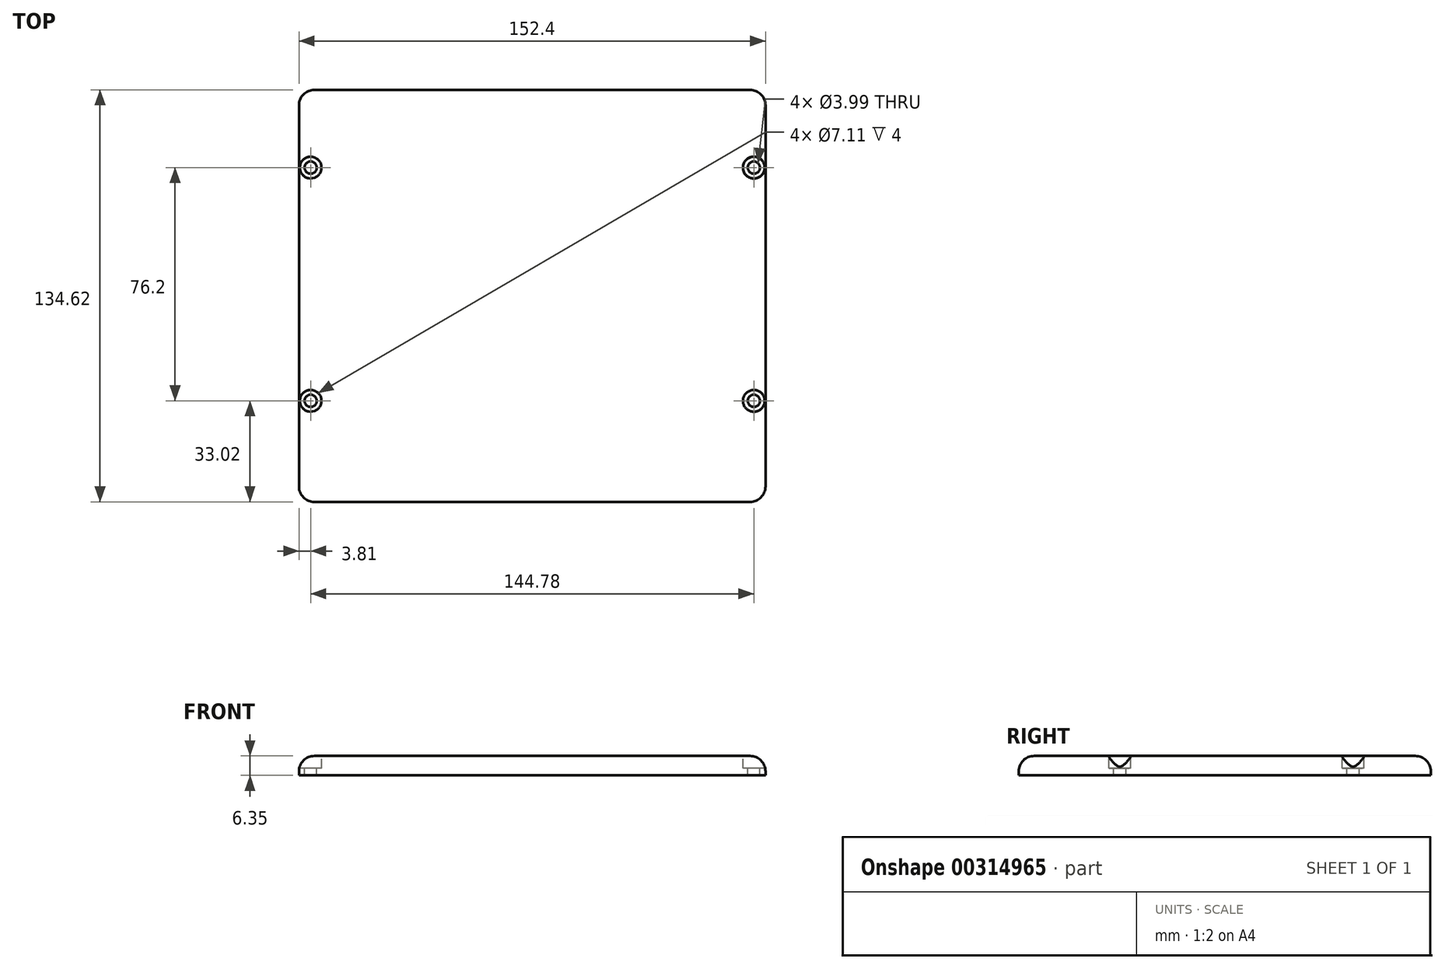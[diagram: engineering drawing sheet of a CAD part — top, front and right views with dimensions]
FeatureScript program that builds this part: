
annotation { "Feature Type Name" : "Feature", "Feature Type Description" : "" }
export const myFeature = defineFeature(function(context is Context, id is Id, definition is map)
    precondition{}
    {
        {
            var Q0;
            Q0=qCreatedBy(makeId("Top.planeOp"),FACE);
            var sketch = newSketch(context, id + "F0", { "sketchPlane" : qUnion([Q0])});
            skLineSegment(sketch, "E0.bottom", {"start": v(76.2, -67.31) * mm, "end": v(-76.2, -67.31) * mm});
            skLineSegment(sketch, "E0.top", {"start": v(76.2, 67.31) * mm, "end": v(-76.2, 67.3) * mm});
            skLineSegment(sketch, "E0.left", {"start": v(76.2, -67.31) * mm, "end": v(76.2, 67.31) * mm});
            skLineSegment(sketch, "E0.right", {"start": v(-76.2, -67.31) * mm, "end": v(-76.2, 67.3) * mm});
            skPoint(sketch, "E0.middle", {"position": v(0, 0) * mm});
            skSolve(sketch);
        }
        {
            var Q0;
            Q0=qSketchRegion(id+"F0",true);
            extrude(context, id + "F1", {"entities" : qUnion([Q0]), "depth" : 6.35 * mm});
        }
        {
            var Q0;
            Q0=makeQuery(id+"F1.opExtrude","CAP_FACE",FACE,{"disambiguationData":[OSD([sQuery(id+"F0.wireOp",EDGE,"E0.bottom"),sQuery(id+"F0.wireOp",EDGE,"E0.top"),sQuery(id+"F0.wireOp",EDGE,"E0.left"),sQuery(id+"F0.wireOp",EDGE,"E0.right")])],"isStart":false});
            var sketch = newSketch(context, id + "F2", { "sketchPlane" : qUnion([Q0])});
            skPoint(sketch, "E1", {"position": v(-72.39, 41.9) * mm});
            skPoint(sketch, "E2", {"position": v(72.4, 41.9) * mm});
            skPoint(sketch, "E3", {"position": v(72.4, -34.3) * mm});
            skPoint(sketch, "E4", {"position": v(-72.39, -34.3) * mm});
            skSolve(sketch);
        }
        {
            var Q0;
            Q0=sQuery(id+"F2.wireOp",VERTEX,"E1");
            var Q1;
            Q1=sQuery(id+"F2.wireOp",VERTEX,"E4");
            var Q2;
            Q2=sQuery(id+"F2.wireOp",VERTEX,"E3");
            var Q3;
            Q3=sQuery(id+"F2.wireOp",VERTEX,"E2");
            var Q4;
            Q4=sQuery(id+"F2.wireOp",VERTEX,"32dfac95-dade-4f80-9e21-36db3b3072a5");
            var Q5;
            Q5=makeQuery(id+"F1.opExtrude","SWEPT_BODY",BODY,{"disambiguationData":[OSD([sQuery(id+"F0.wireOp",EDGE,"E0.bottom"),sQuery(id+"F0.wireOp",EDGE,"E0.top"),sQuery(id+"F0.wireOp",EDGE,"E0.left"),sQuery(id+"F0.wireOp",EDGE,"E0.right")])]});
            hole(context, id + "F3", {"style" : HoleStyle.C_BORE, "endStyle" : HoleEndStyle.THROUGH, "holeDiameter" : 4 * mm, "cBoreDiameter" : 7.11 * mm, "cBoreDepth" : 4 * mm, "tappedDepth" : 12.7 * mm, "tapClearance" : 3, "locations" : qUnion([Q0, Q1, Q2, Q3, Q4]), "scope" : qUnion([Q5])});
        }
        {
            var Q0;
            Q0=makeQuery(id+"F1.opExtrude","CAP_EDGE",EDGE,{"disambiguationData":[OSD([sQuery(id+"F0.wireOp",EDGE,"E0.right")])],"isStart":false});
            var Q1;
            Q1=makeQuery(id+"F1.opExtrude","CAP_EDGE",EDGE,{"disambiguationData":[OSD([sQuery(id+"F0.wireOp",EDGE,"E0.top")])],"isStart":false});
            var Q2;
            Q2=makeQuery(id+"F1.opExtrude","CAP_EDGE",EDGE,{"disambiguationData":[OSD([sQuery(id+"F0.wireOp",EDGE,"E0.bottom")])],"isStart":false});
            var Q3;
            Q3=makeQuery(id+"F1.opExtrude","CAP_EDGE",EDGE,{"disambiguationData":[OSD([sQuery(id+"F0.wireOp",EDGE,"E0.left")])],"isStart":false});
            var Q4;
            Q4=makeQuery(id+"F1.opExtrude","SWEPT_EDGE",EDGE,{"disambiguationData":[OSD([sQuery(id+"F0.wireOp",EDGE,"E0.bottom"),sQuery(id+"F0.wireOp",EDGE,"E0.right")])]});
            var Q5;
            Q5=makeQuery(id+"F1.opExtrude","SWEPT_EDGE",EDGE,{"disambiguationData":[OSD([sQuery(id+"F0.wireOp",EDGE,"E0.bottom"),sQuery(id+"F0.wireOp",EDGE,"E0.left")])]});
            var Q6;
            Q6=makeQuery(id+"F1.opExtrude","SWEPT_EDGE",EDGE,{"disambiguationData":[OSD([sQuery(id+"F0.wireOp",EDGE,"E0.top"),sQuery(id+"F0.wireOp",EDGE,"E0.left")])]});
            var Q7;
            Q7=makeQuery(id+"F1.opExtrude","SWEPT_EDGE",EDGE,{"disambiguationData":[OSD([sQuery(id+"F0.wireOp",EDGE,"E0.top"),sQuery(id+"F0.wireOp",EDGE,"E0.right")])]});
            fillet(context, id + "F4", {"entities" : qUnion([Q0, Q1, Q2, Q3, Q4, Q5, Q6, Q7]), "radius" : 5.08 * mm, "tangentPropagation" : true, "allowEdgeOverflow" : false});
        }
    });
